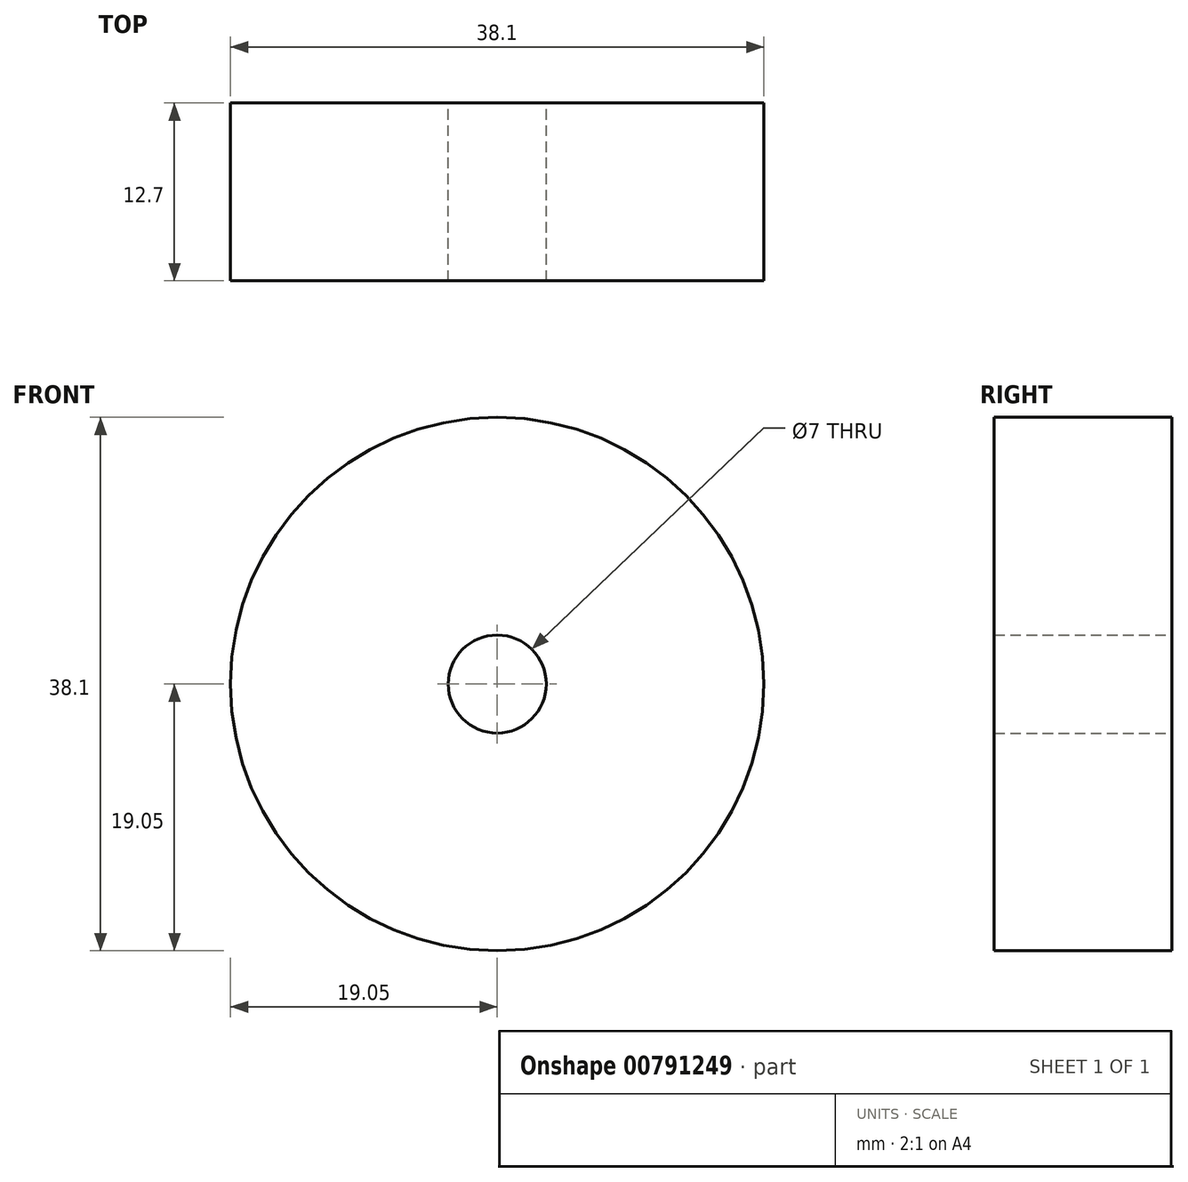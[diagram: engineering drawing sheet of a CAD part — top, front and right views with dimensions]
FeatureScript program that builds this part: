
annotation { "Feature Type Name" : "Feature", "Feature Type Description" : "" }
export const myFeature = defineFeature(function(context is Context, id is Id, definition is map)
    precondition{}
    {
        {
            var Q0;
            Q0=qCreatedBy(makeId("Front.planeOp"),FACE);
            var sketch = newSketch(context, id + "F0", { "sketchPlane" : qUnion([Q0])});
            skCircle(sketch, "E0", {"center": v(0, 0) * mm, "radius": 19.05 * mm});
            skCircle(sketch, "E1", {"center": v(0, 0) * mm, "radius": 3.5 * mm});
            skSolve(sketch);
        }
        {
            var Q0;
            Q0 = qSketchRegion(id + "F0", true);
            extrude(context, id + "F1", {"entities" : qUnion([Q0]), "depth" : 12.7 * mm, "offsetDistance" : 25 * mm});
        }
    });
